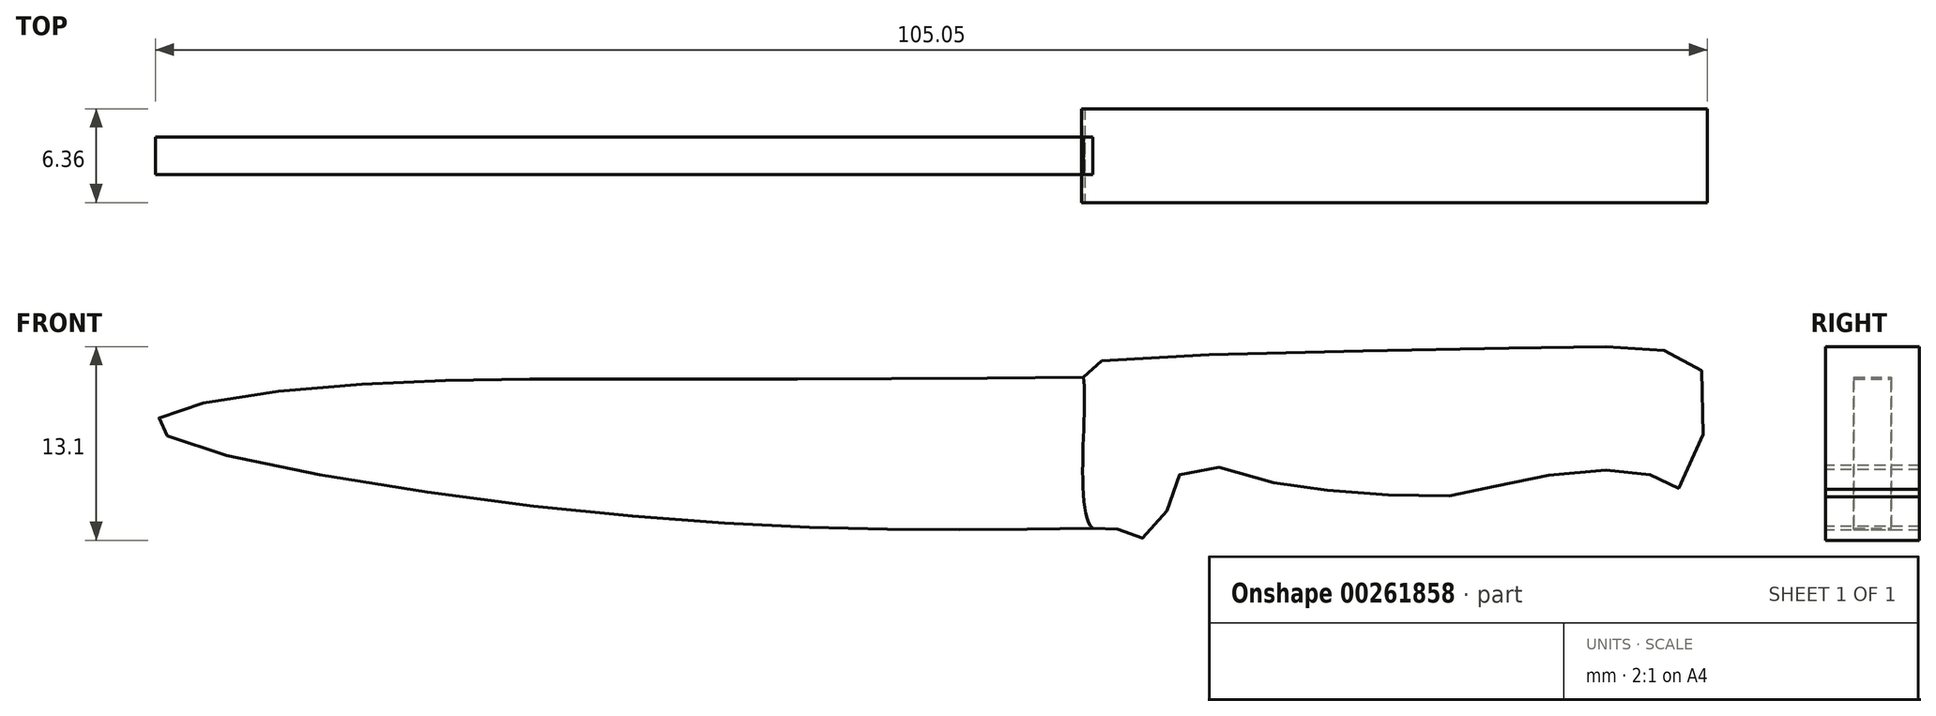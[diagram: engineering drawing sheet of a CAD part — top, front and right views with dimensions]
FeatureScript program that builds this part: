
annotation { "Feature Type Name" : "Feature", "Feature Type Description" : "" }
export const myFeature = defineFeature(function(context is Context, id is Id, definition is map)
    precondition{}
    {
        {
            var Q0;
            Q0=qCreatedBy(makeId("Front.planeOp"),FACE);
            var sketch = newSketch(context, id + "F0", { "sketchPlane" : qUnion([Q0])});
            skFitSpline(sketch, "E0", {"points": [v(11.14, -5.77) * mm, v(10.52, 4.45) * mm, v(10.52, 5.32) * mm, v(39.6, 6.42) * mm, v(50.13, 6.2) * mm, v(52.65, 4.08) * mm, v(50.8, -3.06) * mm, v(49.2, -2.32) * mm, v(45.76, -1.83) * mm, v(39.72, -2.57) * mm, v(35.53, -3.55) * mm, v(28.5, -3.3) * mm, v(22.84, -2.57) * mm, v(17.91, -1.58) * mm, v(16.31, -3.55) * mm, v(15.57, -5.9) * mm, v(12.99, -6.39) * mm, v(12.74, -5.65) * mm, v(11.14, -5.77) * mm]});
            skFitSpline(sketch, "E1", {"points": [v(10.52, 4.45) * mm, v(-18.3, 4.32) * mm, v(-41.84, 3.71) * mm, v(-52.3, 1.25) * mm, v(-32.35, -3.55) * mm, v(-4.44, -5.81) * mm, v(11.14, -5.77) * mm], "startDerivative": vector(-150.42, -1.31) * mm, "endDerivative": vector(101.65, 1.66) * mm});
            skSolve(sketch);
        }
        {
            var Q0;
            Q0=makeQuery(id+"F0.imprint","IMPRINT",FACE,{"disambiguationData":[TD([[makeQuery(id+"F0.imprint","IMPRINT",EDGE,{"derivedFrom":sQuery(id+"F0.wireOp",EDGE,"df16e296-6f95-46a3-a09d-86f3b28c45ac")}),-1.0]])]});
            var Q1;
            {var subQ0=sQuery(id+"F0.wireOp",EDGE,"E1");var subQ1=sQuery(id+"F0.wireOp",EDGE,"E0");var subQ2=makeQuery(id+"F0.imprint","INTERSECT",VERTEX,{"disambiguationData":[OD(0.0)],"derivedFrom":[subQ1,subQ0]});Q1=makeQuery(id+"F0.imprint","IMPRINT",FACE,{"disambiguationData":[TD([[makeQuery(id+"F0.imprint","IMPRINT",EDGE,{"disambiguationData":[TD([[subQ2,1.0]])],"derivedFrom":subQ1}),-1.0]])]});}
            extrude(context, id + "F1", {"entities" : qUnion([Q0, Q1]), "endBound" : BoundingType.SYMMETRIC, "depth" : 6.35 * mm});
        }
        {
            var Q0;
            {var subQ0=sQuery(id+"F0.wireOp",EDGE,"E1");Q0=makeQuery(id+"F0.imprint","IMPRINT",FACE,{"disambiguationData":[TD([[makeQuery(id+"F0.imprint","IMPRINT",EDGE,{"derivedFrom":subQ0}),1.0]])]});}
            extrude(context, id + "F2", {"entities" : qUnion([Q0]), "endBound" : BoundingType.SYMMETRIC, "depth" : 2.54 * mm});
        }
    });
